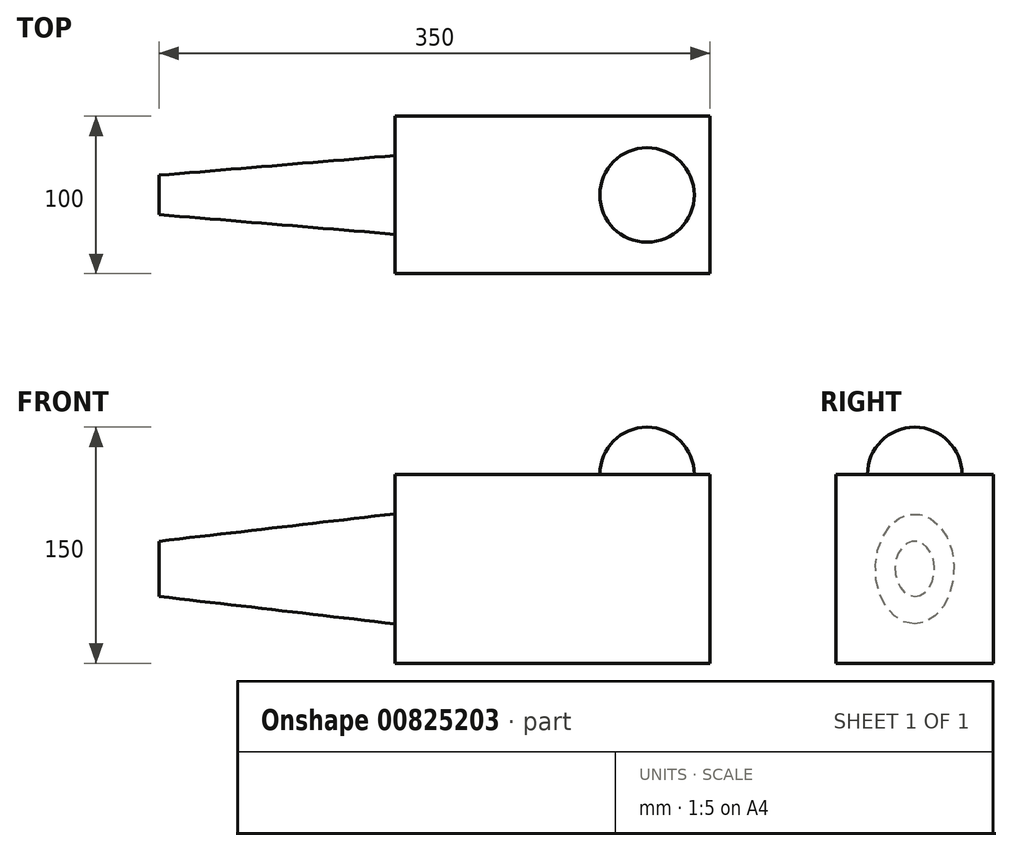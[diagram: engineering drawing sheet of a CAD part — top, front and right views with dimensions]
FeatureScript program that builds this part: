
annotation { "Feature Type Name" : "Feature", "Feature Type Description" : "" }
export const myFeature = defineFeature(function(context is Context, id is Id, definition is map)
    precondition{}
    {
        {
            var Q0;
            Q0=qCreatedBy(makeId("Top.planeOp"),FACE);
            var sketch = newSketch(context, id + "F0", { "sketchPlane" : qUnion([Q0])});
            skLineSegment(sketch, "E0.bottom", {"start": v(100, -50) * mm, "end": v(-100, -50) * mm});
            skLineSegment(sketch, "E0.top", {"start": v(100, 50) * mm, "end": v(-100, 50) * mm});
            skLineSegment(sketch, "E0.left", {"start": v(100, -50) * mm, "end": v(100, 50) * mm});
            skLineSegment(sketch, "E0.right", {"start": v(-100, -50) * mm, "end": v(-100, 50) * mm});
            skPoint(sketch, "E0.middle", {"position": v(0, 0) * mm});
            skSolve(sketch);
        }
        {
            var Q0;
            Q0=makeQuery(id+"F0.imprint","IMPRINT",FACE,{"disambiguationData":[TD([[makeQuery(id+"F0.imprint","IMPRINT",EDGE,{"derivedFrom":sQuery(id+"F0.wireOp",EDGE,"E0.bottom")}),-1.0]])]});
            extrude(context, id + "F1", {"entities" : qUnion([Q0]), "depth" : 120 * mm, "offsetDistance" : 25 * mm});
        }
        {
            var Q0;
            Q0=makeQuery(id+"F1.opExtrude","CAP_FACE",FACE,{"disambiguationData":[OSD([sQuery(id+"F0.wireOp",EDGE,"E0.bottom"),sQuery(id+"F0.wireOp",EDGE,"E0.top"),sQuery(id+"F0.wireOp",EDGE,"E0.left"),sQuery(id+"F0.wireOp",EDGE,"E0.right")])],"isStart":false});
            var sketch = newSketch(context, id + "F2", { "sketchPlane" : qUnion([Q0])});
            skLineSegment(sketch, "E1", {"start": v(-100, 0) * mm, "end": v(100, 0) * mm, "construction": true});
            skArc(sketch, "E2", {"start": v(60, -30) * mm, "mid": v(90, 0) * mm, "end": v(60, 30) * mm});
            skLineSegment(sketch, "E3", {"start": v(60, 0) * mm, "end": v(60, 30) * mm});
            skLineSegment(sketch, "E4", {"start": v(60, 30) * mm, "end": v(60, -30) * mm});
            skSolve(sketch);
        }
        {
            var Q0;
            {var subQ0=sQuery(id+"F2.wireOp",EDGE,"E2");Q0=makeQuery(id+"F2.imprint","IMPRINT",FACE,{"disambiguationData":[TD([[makeQuery(id+"F2.imprint","IMPRINT",EDGE,{"derivedFrom":subQ0}),1.0]])]});}
            var Q1;
            Q1=sQuery(id+"F2.wireOp",EDGE,"E4");
            revolve(context, id + "F3", {"surfaceOperationType" : NewSurfaceOperationType.NEW, "entities" : qUnion([Q0]), "axis" : qUnion([Q1]), "revolveType" : RevolveType.ONE_DIRECTION, "angle" : 180 * degree});
        }
        {
            var Q0;
            Q0=makeQuery(id+"F1.opExtrude","SWEPT_FACE",FACE,{"disambiguationData":[OSD([sQuery(id+"F0.wireOp",EDGE,"E0.right")])]});
            var sketch = newSketch(context, id + "F4", { "sketchPlane" : qUnion([Q0])});
            skLineSegment(sketch, "E5", {"start": v(-50, 60) * mm, "end": v(50, 60) * mm, "construction": true});
            skEllipse(sketch, "E6", {"center": v(0, 60) * mm, "majorRadius": 35 * mm, "minorRadius": 25 * mm, "majorAxis": v(0, -1)});
            skSolve(sketch);
        }
        {
            var Q0;
            Q0=qCreatedBy(makeId("Right.planeOp"),FACE);
            cPlane(context, id + "F5", {"entities" : qUnion([Q0]), "cplaneType" : CPlaneType.OFFSET, "offset" : 250 * mm, "oppositeDirection" : true, "width" : 150 * mm, "height" : 150 * mm});
        }
        {
            var Q0;
            Q0=qCreatedBy(id+"F5.planeOp",FACE);
            var sketch = newSketch(context, id + "F6", { "sketchPlane" : qUnion([Q0])});
            skEllipse(sketch, "E7", {"center": v(0, 60) * mm, "majorRadius": 17.5 * mm, "minorRadius": 12.5 * mm, "majorAxis": v(0, -1)});
            skSolve(sketch);
        }
        {
            var Q1;
            Q1=makeQuery(id+"F4.imprint","IMPRINT",FACE,{"disambiguationData":[TD([[makeQuery(id+"F4.imprint","IMPRINT",EDGE,{"derivedFrom":sQuery(id+"F4.wireOp",EDGE,"E6")}),1.0]])]});
            var Q2;
            Q2=makeQuery(id+"F6.imprint","IMPRINT",FACE,{"disambiguationData":[TD([[makeQuery(id+"F6.imprint","IMPRINT",EDGE,{"derivedFrom":sQuery(id+"F6.wireOp",EDGE,"E7")}),1.0]])]});
            loft(context, id + "F7", {"operationType" : NewBodyOperationType.ADD, "sheetProfilesArray" : [{ "sheetProfileEntities" : qUnion([Q1]) }, { "sheetProfileEntities" : qUnion([Q2]) }]});
        }
    });
